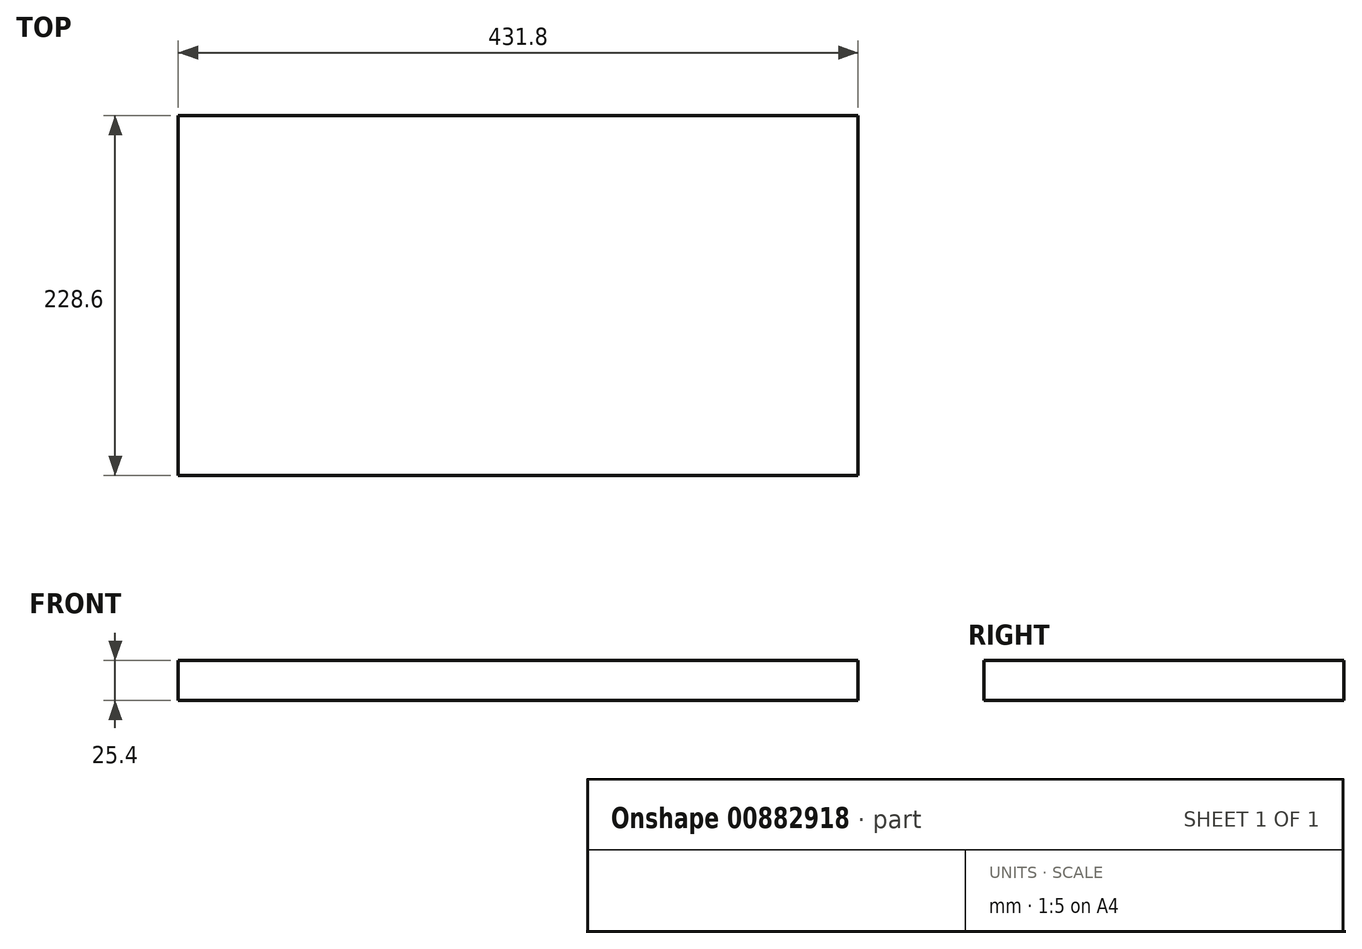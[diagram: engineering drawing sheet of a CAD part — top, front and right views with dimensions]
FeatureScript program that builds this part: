
annotation { "Feature Type Name" : "Feature", "Feature Type Description" : "" }
export const myFeature = defineFeature(function(context is Context, id is Id, definition is map)
    precondition{}
    {
        {
            var Q0;
            Q0=qCreatedBy(makeId("Top.planeOp"),FACE);
            var sketch = newSketch(context, id + "F0", { "sketchPlane" : qUnion([Q0])});
            skLineSegment(sketch, "E0.bottom", {"start": v(0, 0) * mm, "end": v(431.8, 0) * mm});
            skLineSegment(sketch, "E0.top", {"start": v(0, 228.6) * mm, "end": v(431.8, 228.6) * mm});
            skLineSegment(sketch, "E0.left", {"start": v(0, 0) * mm, "end": v(0, 228.6) * mm});
            skLineSegment(sketch, "E0.right", {"start": v(431.8, 0) * mm, "end": v(431.8, 228.6) * mm});
            skSolve(sketch);
        }
        {
            var Q0;
            Q0=makeQuery(id+"F0.imprint","IMPRINT",FACE,{"disambiguationData":[TD([[makeQuery(id+"F0.imprint","IMPRINT",EDGE,{"derivedFrom":sQuery(id+"F0.wireOp",EDGE,"E0.bottom")}),1.0]])]});
            extrude(context, id + "F1", {"entities" : qUnion([Q0]), "depth" : 25.4 * mm, "offsetDistance" : 25.4 * mm});
        }
    });
